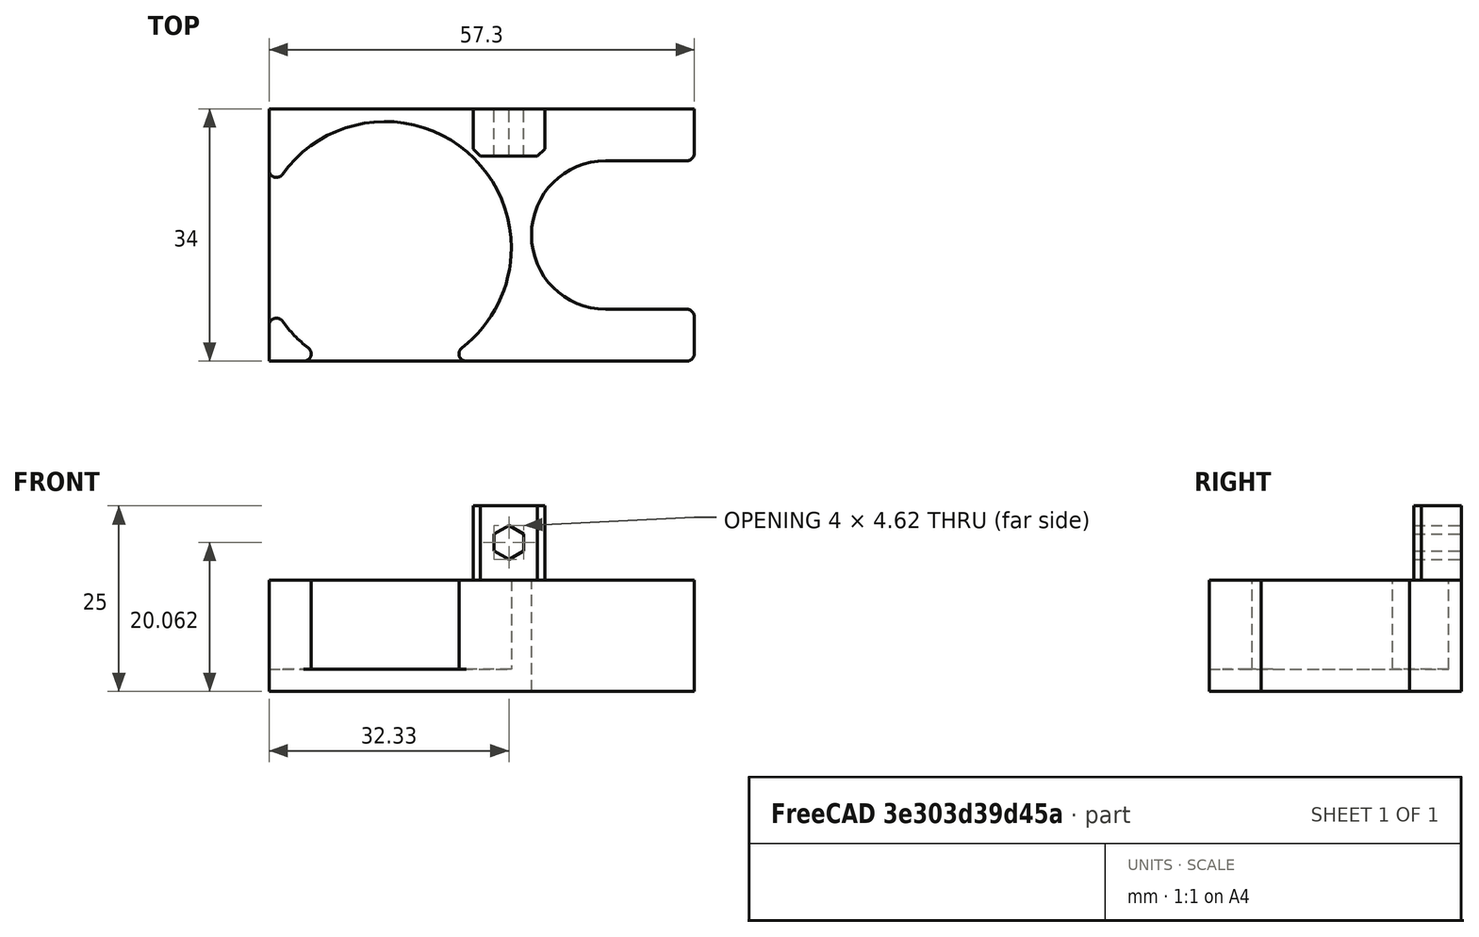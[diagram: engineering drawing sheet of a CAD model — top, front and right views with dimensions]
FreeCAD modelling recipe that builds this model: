
FCSTD DOCUMENT  (FreeCAD 0.19R)
Label: BottleHolder
License: All rights reserved
LicenseURL: http://en.wikipedia.org/wiki/All_rights_reserved
objects: Sketcher::SketchObject×5, PartDesign::Pocket×3, PartDesign::Pad×2, PartDesign::Chamfer×1, PartDesign::Fillet×1, PartDesign::Body×1, Mesh::Feature×1
note: 20 computed .brp shape members not serialized (recipe doc carries the construction recipe); baked Part::Feature solids carry a one-line shape summary decoded from their .brp

FEATURE [Sketcher::SketchObject] Sketch
  FullyConstrained = false
  MapMode = 5
  Support = -> [XY_Plane]
  sketch-geometry (6):
    g0: Circle CenterX=-12.6718 CenterY=-1.71851 CenterZ=0 NormalX=0 NormalY=0 NormalZ=1 AngleXU=0 Radius=17.5
    g1: Circle CenterX=18.5137 CenterY=0 CenterZ=0 NormalX=0 NormalY=0 NormalZ=1 AngleXU=0 Radius=10
    g2: LineSegment StartX=-28.6512 StartY=17 StartZ=0 EndX=28.6512 EndY=17 EndZ=0
    g3: LineSegment StartX=28.6512 StartY=17 StartZ=0 EndX=28.6512 EndY=-17 EndZ=0
    g4: LineSegment StartX=28.6512 StartY=-17 StartZ=0 EndX=-28.6512 EndY=-17 EndZ=0
    g5: LineSegment StartX=-28.6512 StartY=-17 StartZ=0 EndX=-28.6512 EndY=17 EndZ=0
  constraints (12):
    c: PointOnObject(g1,g-1)
    c: Diameter(g1) = 20
    c: Diameter(g0) = 35
    c: Coincident(g2,g3)
    c: Coincident(g3,g4)
    c: Coincident(g4,g5)
    c: Coincident(g5,g2)
    c: Horizontal(g4)
    c: Vertical(g5)
    c: Symmetric(g2,g2,g-2)
    c: Symmetric(g3,g2,g-1)
    c: Distance(g3) = 34
FEATURE [PartDesign::Pad] Pad
  Direction = (1,1,1)
  Length = 15
  Length2 = 100
  Profile = -> Sketch
  Type = 0
FEATURE [Sketcher::SketchObject] Sketch001
  FullyConstrained = false
  MapMode = 5
  Placement = pos=(0,0,15) rot=(0,0,1;0rad)
  Support = -> [Pad]
  sketch-geometry (5):
    g0: Circle CenterX=-13.0155 CenterY=-1.71821 CenterZ=0 NormalX=0 NormalY=0 NormalZ=1 AngleXU=0 Radius=17
    g1: ArcOfCircle CenterX=15.5928 CenterY=0 CenterZ=0 NormalX=0 NormalY=0 NormalZ=1 AngleXU=0 Radius=10 StartAngle=1e-16 EndAngle=3.14159
    g2: ArcOfCircle CenterX=15.5928 CenterY=-26.8037 CenterZ=0 NormalX=0 NormalY=0 NormalZ=1 AngleXU=0 Radius=10 StartAngle=3.14159 EndAngle=6.28319
    g3: LineSegment StartX=5.59278 StartY=1.2e-15 StartZ=0 EndX=5.59278 EndY=-26.8037 EndZ=0
    g4: LineSegment StartX=25.5928 StartY=1.2e-15 StartZ=0 EndX=25.5928 EndY=-26.8037 EndZ=0
  constraints (9):
    c: Diameter(g0) = 34
    c: Tangent(g1,g4) = 1.5708
    c: Tangent(g1,g3) = -1.5708
    c: Tangent(g3,g2) = -1.5708
    c: Tangent(g4,g2) = 1.5708
    c: Vertical(g3)
    c: Equal(g1,g2)
    c: Distance(g1,g1) = 20
    c: PointOnObject(g1,g-1)
FEATURE [PartDesign::Pocket] Pocket
  BaseFeature = -> Pad
  Length = 12
  Length2 = 100
  Profile = -> Sketch001
  Type = 0
FEATURE [Sketcher::SketchObject] Sketch002
  FullyConstrained = false
  MapMode = 5
  Placement = pos=(0,0,15) rot=(0,0,1;0rad)
  Support = -> [Pocket]
  sketch-geometry (4):
    g0: ArcOfCircle CenterX=16.7104 CenterY=0 CenterZ=0 NormalX=0 NormalY=0 NormalZ=1 AngleXU=0 Radius=10 StartAngle=1.5708 EndAngle=4.71239
    g1: ArcOfCircle CenterX=50.3867 CenterY=6e-16 CenterZ=0 NormalX=0 NormalY=0 NormalZ=1 AngleXU=0 Radius=10 StartAngle=4.71239 EndAngle=7.85398
    g2: LineSegment StartX=16.7104 StartY=-10 StartZ=0 EndX=50.3867 EndY=-10 EndZ=0
    g3: LineSegment StartX=16.7104 StartY=10 StartZ=0 EndX=50.3867 EndY=10 EndZ=0
  constraints (8):
    c: Tangent(g0,g3) = 1.5708
    c: Tangent(g0,g2) = -1.5708
    c: Tangent(g2,g1) = -1.5708
    c: Tangent(g3,g1) = 1.5708
    c: Horizontal(g2)
    c: Equal(g0,g1)
    c: PointOnObject(g0,g-1)
    c: Distance(g0,g0) = 20
FEATURE [PartDesign::Pocket] Pocket001
  BaseFeature = -> Pocket
  Length = 15
  Length2 = 100
  Profile = -> Sketch002
  Type = 0
FEATURE [Sketcher::SketchObject] Sketch004
  FullyConstrained = false
  MapMode = 5
  Placement = pos=(0,0,15) rot=(0,0,1;0rad)
  Support = -> [Pocket001]
  sketch-geometry (4):
    g0: LineSegment StartX=-1.15484 StartY=17 StartZ=0 EndX=8.49601 EndY=17 EndZ=0
    g1: LineSegment StartX=8.49601 StartY=17 StartZ=0 EndX=8.49601 EndY=10.6116 EndZ=0
    g2: LineSegment StartX=8.49601 StartY=10.6116 StartZ=0 EndX=-1.15484 EndY=10.6116 EndZ=0
    g3: LineSegment StartX=-1.15484 StartY=10.6116 StartZ=0 EndX=-1.15484 EndY=17 EndZ=0
  constraints (9):
    c: Coincident(g0,g1)
    c: Coincident(g1,g2)
    c: Coincident(g2,g3)
    c: Coincident(g3,g0)
    c: Horizontal(g0)
    c: Horizontal(g2)
    c: Vertical(g1)
    c: Vertical(g3)
    c: DistanceY(g0) = 17
FEATURE [PartDesign::Pad] Pad001
  BaseFeature = -> Pocket001
  Direction = (1,1,1)
  Length = 10
  Length2 = 100
  Profile = -> Sketch004
  Type = 0
FEATURE [Sketcher::SketchObject] Sketch005
  FullyConstrained = false
  MapMode = 5
  Placement = pos=(0,10.6116,0) rot=(1,0,0;1.5708rad)
  Support = -> [Pad001]
  sketch-geometry (7):
    g0: LineSegment StartX=5.68038 StartY=18.9074 StartZ=0 EndX=5.68038 EndY=21.2168 EndZ=0
    g1: LineSegment StartX=5.68038 StartY=21.2168 StartZ=0 EndX=3.68038 EndY=22.3715 EndZ=0
    g2: LineSegment StartX=3.68038 StartY=22.3715 StartZ=0 EndX=1.68038 EndY=21.2168 EndZ=0
    g3: LineSegment StartX=1.68038 StartY=21.2168 StartZ=0 EndX=1.68038 EndY=18.9074 EndZ=0
    g4: LineSegment StartX=1.68038 StartY=18.9074 StartZ=0 EndX=3.68038 EndY=17.7527 EndZ=0
    g5: LineSegment StartX=3.68038 StartY=17.7527 StartZ=0 EndX=5.68038 EndY=18.9074 EndZ=0
    g6: Circle CenterX=3.68038 CenterY=20.0621 CenterZ=0 NormalX=0 NormalY=0 NormalZ=1 AngleXU=0 Radius=2.3094
  constraints (15):
    c: Coincident(g0,g1)
    c: Coincident(g1,g2)
    c: Coincident(g2,g3)
    c: Coincident(g3,g4)
    c: Coincident(g4,g5)
    c: Coincident(g5,g0)
    c: Equal(g0, g1-g5) x5
    c: PointOnObject(g0,g6)
    c: PointOnObject(g1,g6)
    c: PointOnObject(g2,g6)
    c: PointOnObject(g3,g6)
    c: PointOnObject(g4,g6)
    c: PointOnObject(g5,g6)
    c: Vertical(g3)
    c: Distance(g0,g2) = 4
FEATURE [PartDesign::Pocket] Pocket002
  BaseFeature = -> Pad001
  Length = 5
  Length2 = 100
  Profile = -> Sketch005
  Type = 1
FEATURE [PartDesign::Chamfer] Chamfer
  Angle = 45
  Base = -> Pocket002 [Edge57,Edge54]
  BaseFeature = -> Pocket002
  ChamferType = 0
  FlipDirection = false
  Size = 1
  Size2 = 1
  SupportTransform = false
FEATURE [PartDesign::Fillet] Fillet
  Base = -> Chamfer [Edge47,Edge58,Edge60,Edge49,Edge35,Edge44,Edge53]
  BaseFeature = -> Chamfer
  Radius = 1
  SupportTransform = false
FEATURE [PartDesign::Body] Body
  Group = -> [Sketch,Pad,Sketch001,Pocket,Sketch002,Pocket001,Sketch004,Pad001,Sketch005,Pocket002,Chamfer,Fillet]
  Origin = -> Origin
  Tip = -> Fillet
FEATURE [Mesh::Feature] Mesh  label="Fillet (Meshed)"
